# Revit family: Sensor Gooseneck Hob Spout
name_source: partatom
category: Generic Models
units: mm (PartAtom-declared; Revit-internal decimal feet)

## family parameters
Always vertical = Yes
Can host rebar = No
Cut with Voids When Loaded = No
Maintain Annotation Orientation = No
OmniClass Number = 23.31.11.00
Part Type = Normal
Room Calculation Point = No
Round Connector Dimension = Use Diameter
Shared = No
Work Plane-Based = No

## types (1)
- Sensor Gooseneck Hob Spout
    Category = Sensor
    Default Elevation = 0 mm  [stored 0 ft]
    Description = Gooseneck Hob Spout With Spout Tip Sensor
    Keywords = Gooseneck, Sensor, Hob Spout
    Manufacturer = ABI Interiors Pty Ltd
    Model = Brushed Brass(15754), Brushed Copper(15755), Brushed Gunmetal(15756), Matte Black(15758), Stainless Steel(15757)
    Part Number = Brushed Brass(15754), Brushed Copper(15755), Brushed Gunmetal(15756), Matte Black(15758), Stainless Steel(15757)
    Title = Sensor Gooseneck Hob Spout
    URL = https://www.abiinteriors.com.au

note: [stored X ft] marks values corroborated as IEEE doubles in the binary element streams (Revit-internal decimal feet)

## geometry (parser evidence)
native form markers: Sweep x3
no freeform markers — native parametric forms only
